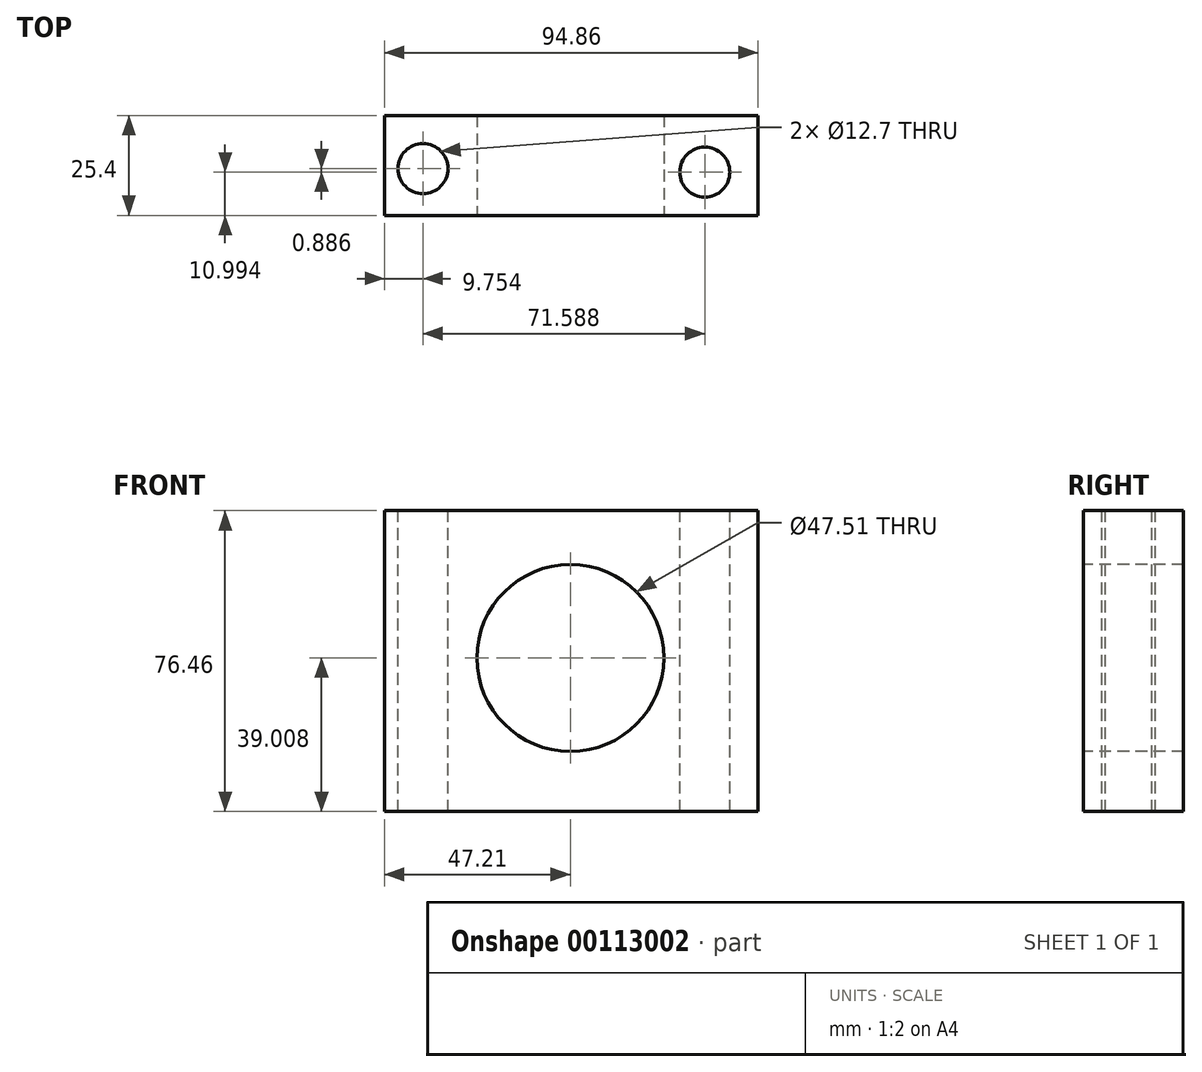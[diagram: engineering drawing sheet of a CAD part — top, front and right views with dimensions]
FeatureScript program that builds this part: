
annotation { "Feature Type Name" : "Feature", "Feature Type Description" : "" }
export const myFeature = defineFeature(function(context is Context, id is Id, definition is map)
    precondition{}
    {
        {
            var Q0;
            Q0=qCreatedBy(makeId("Front.planeOp"),FACE);
            var sketch = newSketch(context, id + "F0", { "sketchPlane" : qUnion([Q0])});
            skLineSegment(sketch, "E0", {"start": v(-60.73, 0) * mm, "end": v(34.13, 0) * mm});
            skLineSegment(sketch, "E1", {"start": v(-60.73, 0) * mm, "end": v(-60.73, 76.46) * mm});
            skLineSegment(sketch, "E2", {"start": v(-60.73, 76.46) * mm, "end": v(34.13, 76.46) * mm});
            skLineSegment(sketch, "E3", {"start": v(34.13, 76.46) * mm, "end": v(34.13, 0) * mm});
            skSolve(sketch);
        }
        {
            var Q0;
            Q0 = qSketchRegion(id + "F0", true);
            extrude(context, id + "F1", {"entities" : qUnion([Q0]), "depth" : 25.4 * mm});
        }
        {
            var Q0;
            Q0=makeQuery(id+"F1.opExtrude","CAP_FACE",FACE,{"disambiguationData":[OSD([sQuery(id+"F0.wireOp",EDGE,"E0"),sQuery(id+"F0.wireOp",EDGE,"E1"),sQuery(id+"F0.wireOp",EDGE,"E2"),sQuery(id+"F0.wireOp",EDGE,"E3")])],"isStart":false});
            var sketch = newSketch(context, id + "F2", { "sketchPlane" : qUnion([Q0])});
            skCircle(sketch, "E4", {"center": v(-13.52, 39) * mm, "radius": 23.76 * mm});
            skSolve(sketch);
        }
        {
            var Q0;
            Q0=makeQuery(id+"F2.imprint","IMPRINT",FACE,{"disambiguationData":[TD([[makeQuery(id+"F2.imprint","IMPRINT",EDGE,{"derivedFrom":sQuery(id+"F2.wireOp",EDGE,"E4")}),1.0]])]});
            extrude(context, id + "F3", {"entities" : qUnion([Q0]), "operationType" : NewBodyOperationType.REMOVE, "endBound" : BoundingType.THROUGH_ALL, "oppositeDirection" : true, "depth" : 25.4 * mm});
        }
        {
            var Q0;
            Q0=makeQuery(id+"F1.opExtrude","SWEPT_FACE",FACE,{"disambiguationData":[OSD([sQuery(id+"F0.wireOp",EDGE,"E2")])]});
            var sketch = newSketch(context, id + "F4", { "sketchPlane" : qUnion([Q0])});
            skCircle(sketch, "E5", {"center": v(-50.98, -13.52) * mm, "radius": 6.35 * mm});
            skCircle(sketch, "E6", {"center": v(20.61, -14.4) * mm, "radius": 6.35 * mm});
            skSolve(sketch);
        }
        {
            var Q0;
            Q0 = qSketchRegion(id + "F4", true);
            extrude(context, id + "F5", {"entities" : qUnion([Q0]), "operationType" : NewBodyOperationType.REMOVE, "oppositeDirection" : true, "depth" : 85.23 * mm});
        }
    });
